# Revit family: Haworth_Planes_TrainingTable_Rectangular2024
name_source: partatom
category: Furniture Systems
revit_build: Autodesk Revit 2018 (Build: 20170223_1515(x64)
units: mm (PartAtom-declared; Revit-internal decimal feet)

## family parameters
Always vertical = Yes
Cut with Voids When Loaded = No
OmniClass Number = 23.40.70.14.64.21
OmniClass Title = Systems Furniture
Part Type = Normal
Room Calculation Point = No
Round Connector Dimension = Use Diameter
Shared = No
Work Plane-Based = No

## types (2) — shared parameters
Actual Height = 29"
Assembly Code = E2020200
Casters = Yes
Center Fliptop Graphic = Yes
Custom Size = No
Cutout = Yes
Cutout Depth = 4"
Cutout Width = 8"
Description = Haworth - Planes Training - Table Rectangular - 20 24
Edgeband = Yes
Flip Top = Yes
Flip Top Depth = 4 3/8"
Flip Top Finish = Haworth _ Paint _ Metallic Champagne
Flip Top Width = 8 1/4"
Fliptop Offset = 8 87/128"
Glides = No
Knife Edge = No
Leg Height = 27 13/16"
Leg Placement = 6 3/16"
Manufacturer = Haworth
Max. Depth = 24"
Max. Width = 96"
Min. Depth = 20"
Min. Width = 36"
Min/Max Depth = 20, 24in.
Min/Max Width = 36-96 in. @ 6 in. increments
Model = TARA
Opening Center = Yes
Opening Left/Right = No
Opening Single = Yes
Opening Single Narrow = No
Opening Single Wide = No
Revision Number = 4
Side Fliptop Graphic = No
Size = Verify Final Dim. w/ Haworth
Support Spacing - From Edge = 7"
Sustainability Info = http://media.haworth.com
Table Thickness = 1 3/16"
URL = www.haworth.com
URL - Product = http://www.haworth.com
Warranty = http://www.haworth.com

## per-type parameters (varying)
| type | Actual Depth | Actual Width | Depth | Side Cutout Offset | Stretcher Width | Width |
| 60w 20d | 20" | 60" | 20" | 20" | 46" | 60" |
| 96w 24d | 24" | 96" | 24" | 32" | 82" | 96" |

## geometry (parser evidence)
native form markers: Sweep x17
no freeform markers — native parametric forms only
